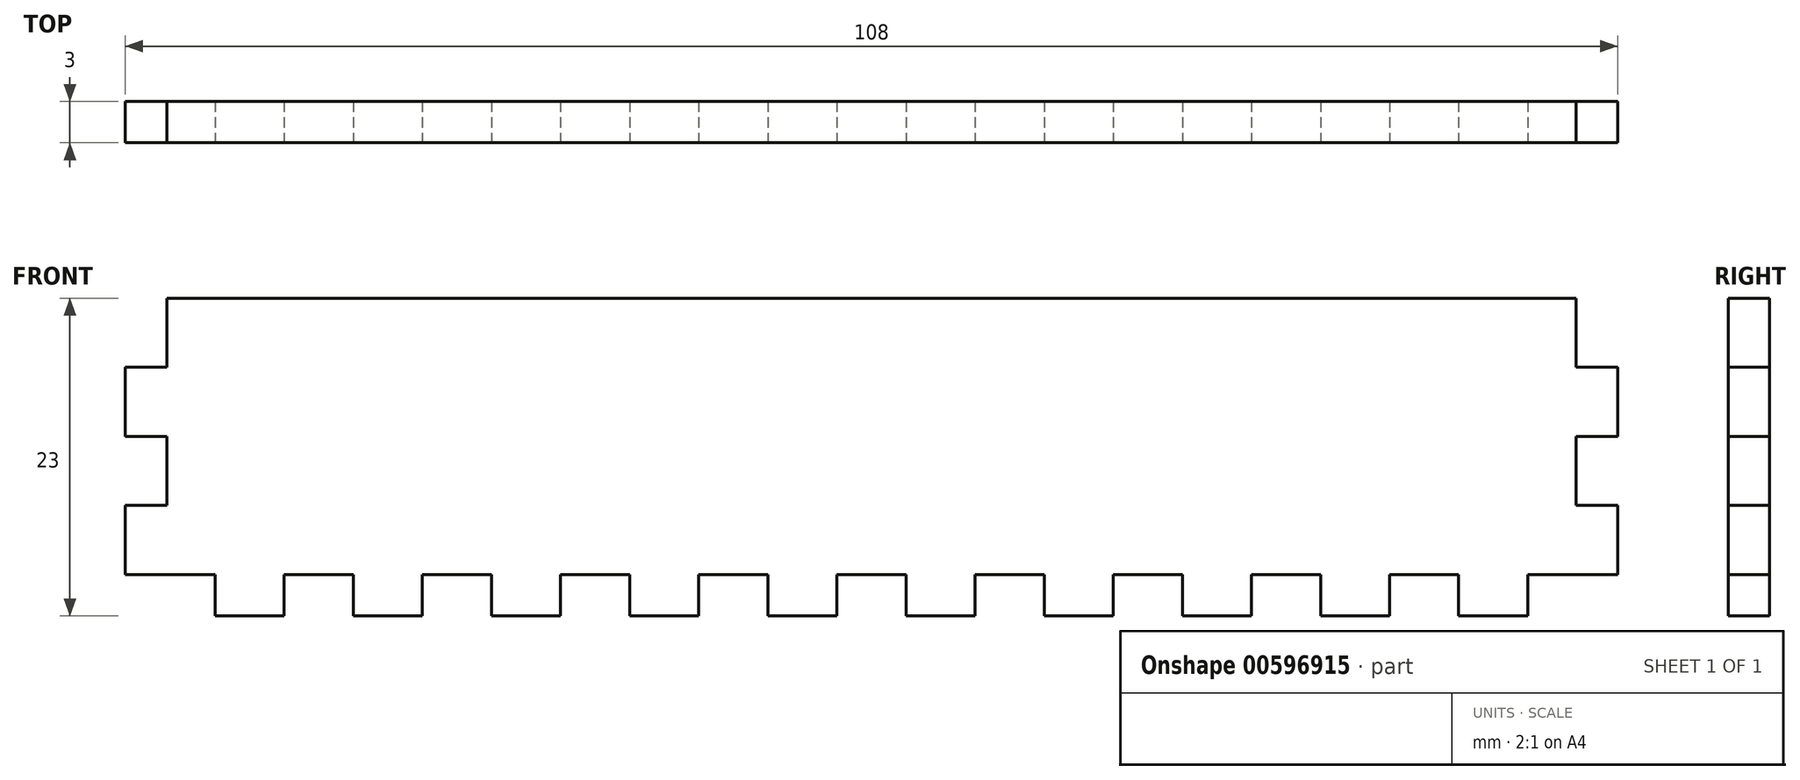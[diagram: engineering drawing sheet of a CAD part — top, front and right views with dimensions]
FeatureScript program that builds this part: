
annotation { "Feature Type Name" : "Feature", "Feature Type Description" : "" }
export const myFeature = defineFeature(function(context is Context, id is Id, definition is map)
    precondition{}
    {
        {
            var Q0;
            Q0=qCreatedBy(makeId("Front.planeOp"),FACE);
            var sketch = newSketch(context, id + "F0", { "sketchPlane" : qUnion([Q0])});
            skLineSegment(sketch, "E0.bottom", {"start": v(51, 20) * mm, "end": v(-51, 20) * mm});
            skLineSegment(sketch, "E0.top", {"start": v(51, -20) * mm, "end": v(-51, -20) * mm});
            skLineSegment(sketch, "E0.left", {"start": v(51, 20) * mm, "end": v(51, -20) * mm});
            skLineSegment(sketch, "E0.right", {"start": v(-51, 20) * mm, "end": v(-51, -20) * mm});
            skPoint(sketch, "E0.middle", {"position": v(0, 0) * mm});
            skSolve(sketch);
        }
        {
            var Q0;
            Q0=qSketchRegion(id+"F0",true);
            extrude(context, id + "F1", {"entities" : qUnion([Q0]), "depth" : 3 * mm, "offsetDistance" : 25 * mm});
        }
        {
            var Q0;
            Q0=makeQuery(id+"F1.opExtrude","CAP_FACE",FACE,{"disambiguationData":[OSD([sQuery(id+"F0.wireOp",EDGE,"E0.bottom"),sQuery(id+"F0.wireOp",EDGE,"E0.top"),sQuery(id+"F0.wireOp",EDGE,"E0.left"),sQuery(id+"F0.wireOp",EDGE,"E0.right")])],"isStart":false});
            var sketch = newSketch(context, id + "F2", { "sketchPlane" : qUnion([Q0])});
            skLineSegment(sketch, "E1.bottom", {"start": v(-51, -20) * mm, "end": v(-54, -20) * mm});
            skLineSegment(sketch, "E1.top", {"start": v(-51, -15) * mm, "end": v(-54, -15) * mm});
            skLineSegment(sketch, "E1.left", {"start": v(-51, -20) * mm, "end": v(-51, -15) * mm});
            skLineSegment(sketch, "E1.right", {"start": v(-54, -20) * mm, "end": v(-54, -15) * mm});
            skLineSegment(sketch, "E2.0.1.0", {"start": v(-51, -5) * mm, "end": v(-54, -5) * mm});
            skLineSegment(sketch, "E2.0.1.1", {"start": v(-54, -10) * mm, "end": v(-54, -5) * mm});
            skLineSegment(sketch, "E2.0.1.2", {"start": v(-51, -10) * mm, "end": v(-51, -5) * mm});
            skLineSegment(sketch, "E2.0.1.3", {"start": v(-51, -10) * mm, "end": v(-54, -10) * mm});
            skLineSegment(sketch, "E2.0.2.0", {"start": v(-51, 5) * mm, "end": v(-54, 5) * mm});
            skLineSegment(sketch, "E2.0.2.1", {"start": v(-54, 0) * mm, "end": v(-54, 5) * mm});
            skLineSegment(sketch, "E2.0.2.2", {"start": v(-51, 0) * mm, "end": v(-51, 5) * mm});
            skLineSegment(sketch, "E2.0.2.3", {"start": v(-51, 0) * mm, "end": v(-54, 0) * mm});
            skLineSegment(sketch, "E2.0.3.0", {"start": v(-51, 15) * mm, "end": v(-54, 15) * mm});
            skLineSegment(sketch, "E2.0.3.1", {"start": v(-54, 10) * mm, "end": v(-54, 15) * mm});
            skLineSegment(sketch, "E2.0.3.2", {"start": v(-51, 10) * mm, "end": v(-51, 15) * mm});
            skLineSegment(sketch, "E2.0.3.3", {"start": v(-51, 10) * mm, "end": v(-54, 10) * mm});
            skLineSegment(sketch, "E2.direction1", {"start": v(-54, -15) * mm, "end": v(-29, -15) * mm, "construction": true});
            skLineSegment(sketch, "E2.direction2", {"start": v(-54, -15) * mm, "end": v(-54, -5) * mm, "construction": true});
            skLineSegment(sketch, "E3.MirrorCS", {"start": v(54, -10) * mm, "end": v(54, -5) * mm});
            skLineSegment(sketch, "E4.MirrorCS", {"start": v(51, -5) * mm, "end": v(54, -5) * mm});
            skLineSegment(sketch, "E5.MirrorCS", {"start": v(51, -20) * mm, "end": v(51, -15) * mm});
            skLineSegment(sketch, "E6.MirrorCS", {"start": v(54, 10) * mm, "end": v(54, 15) * mm});
            skLineSegment(sketch, "E7.MirrorCS", {"start": v(51, -20) * mm, "end": v(54, -20) * mm});
            skLineSegment(sketch, "E8.MirrorCS", {"start": v(51, -15) * mm, "end": v(54, -15) * mm});
            skLineSegment(sketch, "E9.MirrorCS", {"start": v(54, -20) * mm, "end": v(54, -15) * mm});
            skLineSegment(sketch, "E10.MirrorCS", {"start": v(51, 15) * mm, "end": v(54, 15) * mm});
            skLineSegment(sketch, "E11.MirrorCS", {"start": v(51, 10) * mm, "end": v(54, 10) * mm});
            skLineSegment(sketch, "E12.MirrorCS", {"start": v(54, -15) * mm, "end": v(54, -5) * mm, "construction": true});
            skLineSegment(sketch, "E13.MirrorCS", {"start": v(51, 10) * mm, "end": v(51, 15) * mm});
            skLineSegment(sketch, "E14.MirrorCS", {"start": v(54, 0) * mm, "end": v(54, 5) * mm});
            skLineSegment(sketch, "E15.MirrorCS", {"start": v(51, 0) * mm, "end": v(51, 5) * mm});
            skLineSegment(sketch, "E16.MirrorCS", {"start": v(51, 0) * mm, "end": v(54, 0) * mm});
            skLineSegment(sketch, "E17.MirrorCS", {"start": v(51, -10) * mm, "end": v(51, -5) * mm});
            skLineSegment(sketch, "E18.MirrorCS", {"start": v(51, -10) * mm, "end": v(54, -10) * mm});
            skLineSegment(sketch, "E19.MirrorCS", {"start": v(51, 5) * mm, "end": v(54, 5) * mm});
            skSolve(sketch);
        }
        {
            var Q0;
            Q0=qSketchRegion(id+"F2",true);
            extrude(context, id + "F3", {"entities" : qUnion([Q0]), "operationType" : NewBodyOperationType.ADD, "oppositeDirection" : true, "depth" : 3 * mm, "offsetDistance" : 25 * mm});
        }
        {
            var Q0;
            Q0=makeQuery(id+"F3.boolean.opBoolean","MERGE",FACE,{"derivedFrom":[makeQuery(id+"F1.opExtrude","CAP_FACE",FACE,{"disambiguationData":[OSD([sQuery(id+"F0.wireOp",EDGE,"E0.bottom"),sQuery(id+"F0.wireOp",EDGE,"E0.top"),sQuery(id+"F0.wireOp",EDGE,"E0.left"),sQuery(id+"F0.wireOp",EDGE,"E0.right")])],"isStart":false}),makeQuery(id+"F3.opExtrude","CAP_FACE",FACE,{"disambiguationData":[OSD([sQuery(id+"F2.wireOp",EDGE,"E1.bottom"),sQuery(id+"F2.wireOp",EDGE,"E1.top"),sQuery(id+"F2.wireOp",EDGE,"E1.left"),sQuery(id+"F2.wireOp",EDGE,"E1.right")])],"isStart":true}),makeQuery(id+"F3.opExtrude","CAP_FACE",FACE,{"disambiguationData":[OSD([sQuery(id+"F2.wireOp",EDGE,"E2.0.1.0"),sQuery(id+"F2.wireOp",EDGE,"E2.0.1.1"),sQuery(id+"F2.wireOp",EDGE,"E2.0.1.2"),sQuery(id+"F2.wireOp",EDGE,"E2.0.1.3")])],"isStart":true}),makeQuery(id+"F3.opExtrude","CAP_FACE",FACE,{"disambiguationData":[OSD([sQuery(id+"F2.wireOp",EDGE,"E2.0.2.0"),sQuery(id+"F2.wireOp",EDGE,"E2.0.2.1"),sQuery(id+"F2.wireOp",EDGE,"E2.0.2.2"),sQuery(id+"F2.wireOp",EDGE,"E2.0.2.3")])],"isStart":true}),makeQuery(id+"F3.opExtrude","CAP_FACE",FACE,{"disambiguationData":[OSD([sQuery(id+"F2.wireOp",EDGE,"E2.0.3.0"),sQuery(id+"F2.wireOp",EDGE,"E2.0.3.1"),sQuery(id+"F2.wireOp",EDGE,"E2.0.3.2"),sQuery(id+"F2.wireOp",EDGE,"E2.0.3.3")])],"isStart":true}),makeQuery(id+"F3.opExtrude","CAP_FACE",FACE,{"disambiguationData":[OSD([sQuery(id+"F2.wireOp",EDGE,"E3.MirrorCS"),sQuery(id+"F2.wireOp",EDGE,"E4.MirrorCS"),sQuery(id+"F2.wireOp",EDGE,"E17.MirrorCS"),sQuery(id+"F2.wireOp",EDGE,"E18.MirrorCS")])],"isStart":true}),makeQuery(id+"F3.opExtrude","CAP_FACE",FACE,{"disambiguationData":[OSD([sQuery(id+"F2.wireOp",EDGE,"E5.MirrorCS"),sQuery(id+"F2.wireOp",EDGE,"E7.MirrorCS"),sQuery(id+"F2.wireOp",EDGE,"E8.MirrorCS"),sQuery(id+"F2.wireOp",EDGE,"E9.MirrorCS")])],"isStart":true}),makeQuery(id+"F3.opExtrude","CAP_FACE",FACE,{"disambiguationData":[OSD([sQuery(id+"F2.wireOp",EDGE,"E6.MirrorCS"),sQuery(id+"F2.wireOp",EDGE,"E10.MirrorCS"),sQuery(id+"F2.wireOp",EDGE,"E11.MirrorCS"),sQuery(id+"F2.wireOp",EDGE,"E13.MirrorCS")])],"isStart":true}),makeQuery(id+"F3.opExtrude","CAP_FACE",FACE,{"disambiguationData":[OSD([sQuery(id+"F2.wireOp",EDGE,"E14.MirrorCS"),sQuery(id+"F2.wireOp",EDGE,"E15.MirrorCS"),sQuery(id+"F2.wireOp",EDGE,"E16.MirrorCS"),sQuery(id+"F2.wireOp",EDGE,"E19.MirrorCS")])],"isStart":true})]});
            var sketch = newSketch(context, id + "F4", { "sketchPlane" : qUnion([Q0])});
            skLineSegment(sketch, "E20", {"start": v(0, -20) * mm, "end": v(0, -23) * mm, "construction": true});
            skPoint(sketch, "E20.endSnap0", {"position": v(0, -20) * mm});
            skLineSegment(sketch, "E21", {"start": v(0, -23) * mm, "end": v(2.5, -23) * mm, "construction": true});
            skLineSegment(sketch, "E22.bottom", {"start": v(2.5, -23) * mm, "end": v(7.5, -23) * mm});
            skLineSegment(sketch, "E22.top", {"start": v(2.5, -20) * mm, "end": v(7.5, -20) * mm});
            skLineSegment(sketch, "E22.left", {"start": v(2.5, -23) * mm, "end": v(2.5, -20) * mm});
            skLineSegment(sketch, "E22.right", {"start": v(7.5, -23) * mm, "end": v(7.5, -20) * mm});
            skLineSegment(sketch, "E23.1.0.0", {"start": v(12.5, -23) * mm, "end": v(17.5, -23) * mm});
            skLineSegment(sketch, "E23.1.0.1", {"start": v(12.5, -23) * mm, "end": v(12.5, -20) * mm});
            skLineSegment(sketch, "E23.1.0.2", {"start": v(17.5, -23) * mm, "end": v(17.5, -20) * mm});
            skLineSegment(sketch, "E23.1.0.3", {"start": v(12.5, -20) * mm, "end": v(17.5, -20) * mm});
            skLineSegment(sketch, "E23.2.0.0", {"start": v(22.5, -23) * mm, "end": v(27.5, -23) * mm});
            skLineSegment(sketch, "E23.2.0.1", {"start": v(22.5, -23) * mm, "end": v(22.5, -20) * mm});
            skLineSegment(sketch, "E23.2.0.2", {"start": v(27.5, -23) * mm, "end": v(27.5, -20) * mm});
            skLineSegment(sketch, "E23.2.0.3", {"start": v(22.5, -20) * mm, "end": v(27.5, -20) * mm});
            skLineSegment(sketch, "E23.3.0.0", {"start": v(32.5, -23) * mm, "end": v(37.5, -23) * mm});
            skLineSegment(sketch, "E23.3.0.1", {"start": v(32.5, -23) * mm, "end": v(32.5, -20) * mm});
            skLineSegment(sketch, "E23.3.0.2", {"start": v(37.5, -23) * mm, "end": v(37.5, -20) * mm});
            skLineSegment(sketch, "E23.3.0.3", {"start": v(32.5, -20) * mm, "end": v(37.5, -20) * mm});
            skLineSegment(sketch, "E23.4.0.0", {"start": v(42.5, -23) * mm, "end": v(47.5, -23) * mm});
            skLineSegment(sketch, "E23.4.0.1", {"start": v(42.5, -23) * mm, "end": v(42.5, -20) * mm});
            skLineSegment(sketch, "E23.4.0.2", {"start": v(47.5, -23) * mm, "end": v(47.5, -20) * mm});
            skLineSegment(sketch, "E23.4.0.3", {"start": v(42.5, -20) * mm, "end": v(47.5, -20) * mm});
            skLineSegment(sketch, "E23.direction1", {"start": v(2.5, -23) * mm, "end": v(12.5, -23) * mm, "construction": true});
            skLineSegment(sketch, "E24.MirrorCS", {"start": v(-27.5, -23) * mm, "end": v(-27.5, -20) * mm});
            skLineSegment(sketch, "E25.MirrorCS", {"start": v(-22.5, -23) * mm, "end": v(-22.5, -20) * mm});
            skLineSegment(sketch, "E26.MirrorCS", {"start": v(-17.5, -23) * mm, "end": v(-17.5, -20) * mm});
            skLineSegment(sketch, "E27.MirrorCS", {"start": v(-12.5, -23) * mm, "end": v(-12.5, -20) * mm});
            skLineSegment(sketch, "E28.MirrorCS", {"start": v(-7.5, -23) * mm, "end": v(-7.5, -20) * mm});
            skLineSegment(sketch, "E29.MirrorCS", {"start": v(-2.5, -23) * mm, "end": v(-2.5, -20) * mm});
            skLineSegment(sketch, "E30.MirrorCS", {"start": v(-32.5, -23) * mm, "end": v(-32.5, -20) * mm});
            skLineSegment(sketch, "E31.MirrorCS", {"start": v(-47.5, -23) * mm, "end": v(-47.5, -20) * mm});
            skLineSegment(sketch, "E32.MirrorCS", {"start": v(-37.5, -23) * mm, "end": v(-37.5, -20) * mm});
            skLineSegment(sketch, "E33.MirrorCS", {"start": v(-42.5, -23) * mm, "end": v(-42.5, -20) * mm});
            skLineSegment(sketch, "E34.MirrorCS", {"start": v(-2.5, -23) * mm, "end": v(-7.5, -23) * mm});
            skLineSegment(sketch, "E35.MirrorCS", {"start": v(-32.5, -20) * mm, "end": v(-37.5, -20) * mm});
            skLineSegment(sketch, "E36.MirrorCS", {"start": v(-42.5, -20) * mm, "end": v(-47.5, -20) * mm});
            skLineSegment(sketch, "E37.MirrorCS", {"start": v(-22.5, -23) * mm, "end": v(-27.5, -23) * mm});
            skLineSegment(sketch, "E38.MirrorCS", {"start": v(-12.5, -20) * mm, "end": v(-17.5, -20) * mm});
            skLineSegment(sketch, "E39.MirrorCS", {"start": v(-12.5, -23) * mm, "end": v(-17.5, -23) * mm});
            skLineSegment(sketch, "E40.MirrorCS", {"start": v(-2.5, -20) * mm, "end": v(-7.5, -20) * mm});
            skLineSegment(sketch, "E41.MirrorCS", {"start": v(-32.5, -23) * mm, "end": v(-37.5, -23) * mm});
            skLineSegment(sketch, "E42.MirrorCS", {"start": v(-22.5, -20) * mm, "end": v(-27.5, -20) * mm});
            skLineSegment(sketch, "E43.MirrorCS", {"start": v(-42.5, -23) * mm, "end": v(-47.5, -23) * mm});
            skLineSegment(sketch, "E44.MirrorCS", {"start": v(-2.5, -23) * mm, "end": v(-12.5, -23) * mm, "construction": true});
            skSolve(sketch);
        }
        {
            var Q0;
            Q0=qSketchRegion(id+"F4",true);
            extrude(context, id + "F5", {"entities" : qUnion([Q0]), "operationType" : NewBodyOperationType.ADD, "oppositeDirection" : true, "depth" : 3 * mm, "offsetDistance" : 25 * mm});
        }
        {
            var Q0;
            Q0=makeQuery(id+"F5.boolean.opBoolean","MERGE",FACE,{"derivedFrom":[makeQuery(id+"F3.boolean.opBoolean","MERGE",FACE,{"derivedFrom":[makeQuery(id+"F1.opExtrude","CAP_FACE",FACE,{"disambiguationData":[OSD([sQuery(id+"F0.wireOp",EDGE,"E0.bottom"),sQuery(id+"F0.wireOp",EDGE,"E0.top"),sQuery(id+"F0.wireOp",EDGE,"E0.left"),sQuery(id+"F0.wireOp",EDGE,"E0.right")])],"isStart":false}),makeQuery(id+"F3.opExtrude","CAP_FACE",FACE,{"disambiguationData":[OSD([sQuery(id+"F2.wireOp",EDGE,"E1.bottom"),sQuery(id+"F2.wireOp",EDGE,"E1.top"),sQuery(id+"F2.wireOp",EDGE,"E1.left"),sQuery(id+"F2.wireOp",EDGE,"E1.right")])],"isStart":true}),makeQuery(id+"F3.opExtrude","CAP_FACE",FACE,{"disambiguationData":[OSD([sQuery(id+"F2.wireOp",EDGE,"E2.0.1.0"),sQuery(id+"F2.wireOp",EDGE,"E2.0.1.1"),sQuery(id+"F2.wireOp",EDGE,"E2.0.1.2"),sQuery(id+"F2.wireOp",EDGE,"E2.0.1.3")])],"isStart":true}),makeQuery(id+"F3.opExtrude","CAP_FACE",FACE,{"disambiguationData":[OSD([sQuery(id+"F2.wireOp",EDGE,"E2.0.2.0"),sQuery(id+"F2.wireOp",EDGE,"E2.0.2.1"),sQuery(id+"F2.wireOp",EDGE,"E2.0.2.2"),sQuery(id+"F2.wireOp",EDGE,"E2.0.2.3")])],"isStart":true}),makeQuery(id+"F3.opExtrude","CAP_FACE",FACE,{"disambiguationData":[OSD([sQuery(id+"F2.wireOp",EDGE,"E2.0.3.0"),sQuery(id+"F2.wireOp",EDGE,"E2.0.3.1"),sQuery(id+"F2.wireOp",EDGE,"E2.0.3.2"),sQuery(id+"F2.wireOp",EDGE,"E2.0.3.3")])],"isStart":true}),makeQuery(id+"F3.opExtrude","CAP_FACE",FACE,{"disambiguationData":[OSD([sQuery(id+"F2.wireOp",EDGE,"E3.MirrorCS"),sQuery(id+"F2.wireOp",EDGE,"E4.MirrorCS"),sQuery(id+"F2.wireOp",EDGE,"E17.MirrorCS"),sQuery(id+"F2.wireOp",EDGE,"E18.MirrorCS")])],"isStart":true}),makeQuery(id+"F3.opExtrude","CAP_FACE",FACE,{"disambiguationData":[OSD([sQuery(id+"F2.wireOp",EDGE,"E5.MirrorCS"),sQuery(id+"F2.wireOp",EDGE,"E7.MirrorCS"),sQuery(id+"F2.wireOp",EDGE,"E8.MirrorCS"),sQuery(id+"F2.wireOp",EDGE,"E9.MirrorCS")])],"isStart":true}),makeQuery(id+"F3.opExtrude","CAP_FACE",FACE,{"disambiguationData":[OSD([sQuery(id+"F2.wireOp",EDGE,"E6.MirrorCS"),sQuery(id+"F2.wireOp",EDGE,"E10.MirrorCS"),sQuery(id+"F2.wireOp",EDGE,"E11.MirrorCS"),sQuery(id+"F2.wireOp",EDGE,"E13.MirrorCS")])],"isStart":true}),makeQuery(id+"F3.opExtrude","CAP_FACE",FACE,{"disambiguationData":[OSD([sQuery(id+"F2.wireOp",EDGE,"E14.MirrorCS"),sQuery(id+"F2.wireOp",EDGE,"E15.MirrorCS"),sQuery(id+"F2.wireOp",EDGE,"E16.MirrorCS"),sQuery(id+"F2.wireOp",EDGE,"E19.MirrorCS")])],"isStart":true})]}),makeQuery(id+"F5.opExtrude","CAP_FACE",FACE,{"disambiguationData":[OSD([sQuery(id+"F4.wireOp",EDGE,"E22.bottom"),sQuery(id+"F4.wireOp",EDGE,"E22.top"),sQuery(id+"F4.wireOp",EDGE,"E22.left"),sQuery(id+"F4.wireOp",EDGE,"E22.right")])],"isStart":true}),makeQuery(id+"F5.opExtrude","CAP_FACE",FACE,{"disambiguationData":[OSD([sQuery(id+"F4.wireOp",EDGE,"E23.1.0.0"),sQuery(id+"F4.wireOp",EDGE,"E23.1.0.1"),sQuery(id+"F4.wireOp",EDGE,"E23.1.0.2"),sQuery(id+"F4.wireOp",EDGE,"E23.1.0.3")])],"isStart":true}),makeQuery(id+"F5.opExtrude","CAP_FACE",FACE,{"disambiguationData":[OSD([sQuery(id+"F4.wireOp",EDGE,"E23.2.0.0"),sQuery(id+"F4.wireOp",EDGE,"E23.2.0.1"),sQuery(id+"F4.wireOp",EDGE,"E23.2.0.2"),sQuery(id+"F4.wireOp",EDGE,"E23.2.0.3")])],"isStart":true}),makeQuery(id+"F5.opExtrude","CAP_FACE",FACE,{"disambiguationData":[OSD([sQuery(id+"F4.wireOp",EDGE,"E23.3.0.0"),sQuery(id+"F4.wireOp",EDGE,"E23.3.0.1"),sQuery(id+"F4.wireOp",EDGE,"E23.3.0.2"),sQuery(id+"F4.wireOp",EDGE,"E23.3.0.3")])],"isStart":true}),makeQuery(id+"F5.opExtrude","CAP_FACE",FACE,{"disambiguationData":[OSD([sQuery(id+"F4.wireOp",EDGE,"E23.4.0.0"),sQuery(id+"F4.wireOp",EDGE,"E23.4.0.1"),sQuery(id+"F4.wireOp",EDGE,"E23.4.0.2"),sQuery(id+"F4.wireOp",EDGE,"E23.4.0.3")])],"isStart":true}),makeQuery(id+"F5.opExtrude","CAP_FACE",FACE,{"disambiguationData":[OSD([sQuery(id+"F4.wireOp",EDGE,"E24.MirrorCS"),sQuery(id+"F4.wireOp",EDGE,"E25.MirrorCS"),sQuery(id+"F4.wireOp",EDGE,"E37.MirrorCS"),sQuery(id+"F4.wireOp",EDGE,"E42.MirrorCS")])],"isStart":true}),makeQuery(id+"F5.opExtrude","CAP_FACE",FACE,{"disambiguationData":[OSD([sQuery(id+"F4.wireOp",EDGE,"E26.MirrorCS"),sQuery(id+"F4.wireOp",EDGE,"E27.MirrorCS"),sQuery(id+"F4.wireOp",EDGE,"E38.MirrorCS"),sQuery(id+"F4.wireOp",EDGE,"E39.MirrorCS")])],"isStart":true}),makeQuery(id+"F5.opExtrude","CAP_FACE",FACE,{"disambiguationData":[OSD([sQuery(id+"F4.wireOp",EDGE,"E28.MirrorCS"),sQuery(id+"F4.wireOp",EDGE,"E29.MirrorCS"),sQuery(id+"F4.wireOp",EDGE,"E34.MirrorCS"),sQuery(id+"F4.wireOp",EDGE,"E40.MirrorCS")])],"isStart":true}),makeQuery(id+"F5.opExtrude","CAP_FACE",FACE,{"disambiguationData":[OSD([sQuery(id+"F4.wireOp",EDGE,"E30.MirrorCS"),sQuery(id+"F4.wireOp",EDGE,"E32.MirrorCS"),sQuery(id+"F4.wireOp",EDGE,"E35.MirrorCS"),sQuery(id+"F4.wireOp",EDGE,"E41.MirrorCS")])],"isStart":true}),makeQuery(id+"F5.opExtrude","CAP_FACE",FACE,{"disambiguationData":[OSD([sQuery(id+"F4.wireOp",EDGE,"E31.MirrorCS"),sQuery(id+"F4.wireOp",EDGE,"E33.MirrorCS"),sQuery(id+"F4.wireOp",EDGE,"E36.MirrorCS"),sQuery(id+"F4.wireOp",EDGE,"E43.MirrorCS")])],"isStart":true})]});
            var sketch = newSketch(context, id + "F6", { "sketchPlane" : qUnion([Q0])});
            skLineSegment(sketch, "E45.bottom", {"start": v(-54, 0) * mm, "end": v(55.86, 0) * mm});
            skLineSegment(sketch, "E45.top", {"start": v(-54, 22.12) * mm, "end": v(55.86, 22.12) * mm});
            skLineSegment(sketch, "E45.left", {"start": v(-54, 0) * mm, "end": v(-54, 22.12) * mm});
            skLineSegment(sketch, "E45.right", {"start": v(55.86, 0) * mm, "end": v(55.86, 22.12) * mm});
            skSolve(sketch);
        }
        {
            var Q0;
            Q0 = qSketchRegion(id + "F6", true);
            extrude(context, id + "F7", {"entities" : qUnion([Q0]), "operationType" : NewBodyOperationType.REMOVE, "oppositeDirection" : true, "depth" : 25 * mm, "offsetDistance" : 25 * mm});
        }
    });
